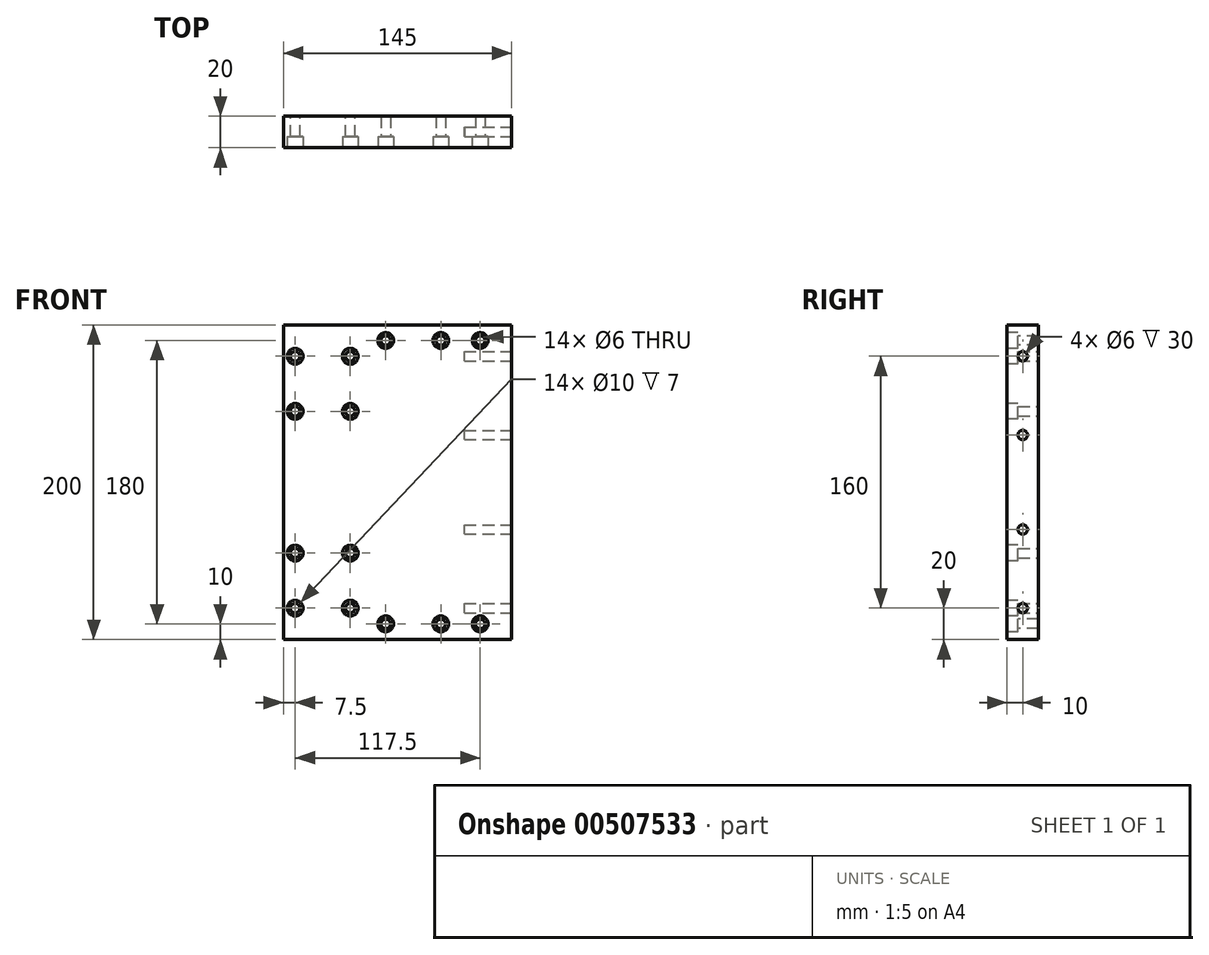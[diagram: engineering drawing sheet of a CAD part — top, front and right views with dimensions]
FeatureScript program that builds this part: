
annotation { "Feature Type Name" : "Feature", "Feature Type Description" : "" }
export const myFeature = defineFeature(function(context is Context, id is Id, definition is map)
    precondition{}
    {
        {
            var Q0;
            Q0=qCreatedBy(makeId("Front.planeOp"),FACE);
            var sketch = newSketch(context, id + "F0", { "sketchPlane" : qUnion([Q0])});
            skLineSegment(sketch, "E0.bottom", {"start": v(0, 0) * mm, "end": v(145, 0) * mm});
            skLineSegment(sketch, "E0.top", {"start": v(0, 200) * mm, "end": v(145, 200) * mm});
            skLineSegment(sketch, "E0.left", {"start": v(0, 0) * mm, "end": v(0, 200) * mm});
            skLineSegment(sketch, "E0.right", {"start": v(145, 0) * mm, "end": v(145, 200) * mm});
            skCircle(sketch, "E1", {"center": v(7.5, 20) * mm, "radius": 3 * mm});
            skCircle(sketch, "E2", {"center": v(7.5, 55) * mm, "radius": 3 * mm});
            skCircle(sketch, "E3", {"center": v(7.5, 145) * mm, "radius": 3 * mm});
            skCircle(sketch, "E4", {"center": v(7.5, 180) * mm, "radius": 3 * mm});
            skCircle(sketch, "E5", {"center": v(42.5, 20) * mm, "radius": 3 * mm});
            skCircle(sketch, "E6", {"center": v(42.5, 55) * mm, "radius": 3 * mm});
            skCircle(sketch, "E7", {"center": v(42.5, 145) * mm, "radius": 3 * mm});
            skCircle(sketch, "E8", {"center": v(42.5, 180) * mm, "radius": 3 * mm});
            skSolve(sketch);
        }
        {
            var Q0;
            Q0=makeQuery(id+"F0.imprint","IMPRINT",FACE,{"disambiguationData":[TD([[makeQuery(id+"F0.imprint","IMPRINT",EDGE,{"derivedFrom":sQuery(id+"F0.wireOp",EDGE,"E0.bottom")}),1.0]])]});
            extrude(context, id + "F1", {"entities" : qUnion([Q0]), "depth" : 20 * mm});
        }
        {
            var Q0;
            Q0=makeQuery(id+"F1.opExtrude","CAP_FACE",FACE,{"disambiguationData":[OSD([sQuery(id+"F0.wireOp",EDGE,"E0.bottom"),sQuery(id+"F0.wireOp",EDGE,"E0.top"),sQuery(id+"F0.wireOp",EDGE,"E0.left"),sQuery(id+"F0.wireOp",EDGE,"E0.right"),sQuery(id+"F0.wireOp",EDGE,"E1"),sQuery(id+"F0.wireOp",EDGE,"E2"),sQuery(id+"F0.wireOp",EDGE,"E3"),sQuery(id+"F0.wireOp",EDGE,"E4"),sQuery(id+"F0.wireOp",EDGE,"E5"),sQuery(id+"F0.wireOp",EDGE,"E6"),sQuery(id+"F0.wireOp",EDGE,"E7"),sQuery(id+"F0.wireOp",EDGE,"E8")])],"isStart":false});
            var sketch = newSketch(context, id + "F2", { "sketchPlane" : qUnion([Q0])});
            skCircle(sketch, "E9", {"center": v(7.5, 180) * mm, "radius": 5 * mm});
            skCircle(sketch, "E10", {"center": v(42.5, 180) * mm, "radius": 5 * mm});
            skCircle(sketch, "E11", {"center": v(7.5, 145) * mm, "radius": 5 * mm});
            skCircle(sketch, "E12", {"center": v(42.5, 145) * mm, "radius": 5 * mm});
            skCircle(sketch, "E13", {"center": v(7.5, 55) * mm, "radius": 5 * mm});
            skCircle(sketch, "E14", {"center": v(42.5, 55) * mm, "radius": 5 * mm});
            skCircle(sketch, "E15", {"center": v(7.5, 20) * mm, "radius": 5 * mm});
            skCircle(sketch, "E16", {"center": v(42.5, 20) * mm, "radius": 5 * mm});
            skSolve(sketch);
        }
        {
            var Q0;
            Q0 = qSketchRegion(id + "F2", true);
            extrude(context, id + "F3", {"entities" : qUnion([Q0]), "operationType" : NewBodyOperationType.REMOVE, "oppositeDirection" : true, "depth" : 7 * mm});
        }
        {
            var Q0;
            Q0=makeQuery(id+"F1.opExtrude","SWEPT_FACE",FACE,{"disambiguationData":[OSD([sQuery(id+"F0.wireOp",EDGE,"E0.right")])]});
            var sketch = newSketch(context, id + "F4", { "sketchPlane" : qUnion([Q0])});
            skCircle(sketch, "E17", {"center": v(-10, 20) * mm, "radius": 3 * mm});
            skCircle(sketch, "E18", {"center": v(-10, 70) * mm, "radius": 3 * mm});
            skCircle(sketch, "E19", {"center": v(-10, 130) * mm, "radius": 3 * mm});
            skCircle(sketch, "E20", {"center": v(-10, 180) * mm, "radius": 3 * mm});
            skSolve(sketch);
        }
        {
            var Q0;
            Q0 = qSketchRegion(id + "F4", true);
            extrude(context, id + "F5", {"entities" : qUnion([Q0]), "operationType" : NewBodyOperationType.REMOVE, "oppositeDirection" : true, "depth" : 30 * mm});
        }
        {
            var Q0;
            Q0=makeQuery(id+"F1.opExtrude","CAP_FACE",FACE,{"disambiguationData":[OSD([sQuery(id+"F0.wireOp",EDGE,"E0.bottom"),sQuery(id+"F0.wireOp",EDGE,"E0.top"),sQuery(id+"F0.wireOp",EDGE,"E0.left"),sQuery(id+"F0.wireOp",EDGE,"E0.right"),sQuery(id+"F0.wireOp",EDGE,"E1"),sQuery(id+"F0.wireOp",EDGE,"E2"),sQuery(id+"F0.wireOp",EDGE,"E3"),sQuery(id+"F0.wireOp",EDGE,"E4"),sQuery(id+"F0.wireOp",EDGE,"E5"),sQuery(id+"F0.wireOp",EDGE,"E6"),sQuery(id+"F0.wireOp",EDGE,"E7"),sQuery(id+"F0.wireOp",EDGE,"E8")])],"isStart":false});
            var sketch = newSketch(context, id + "F6", { "sketchPlane" : qUnion([Q0])});
            skCircle(sketch, "E21", {"center": v(125, 190) * mm, "radius": 3 * mm});
            skCircle(sketch, "E22", {"center": v(100, 190) * mm, "radius": 3 * mm});
            skCircle(sketch, "E23", {"center": v(65, 190) * mm, "radius": 3 * mm});
            skCircle(sketch, "E24", {"center": v(125, 10) * mm, "radius": 3 * mm});
            skCircle(sketch, "E25", {"center": v(100, 10) * mm, "radius": 3 * mm});
            skCircle(sketch, "E26", {"center": v(65, 10) * mm, "radius": 3 * mm});
            skSolve(sketch);
        }
        {
            var Q0;
            Q0 = qSketchRegion(id + "F6", true);
            extrude(context, id + "F7", {"entities" : qUnion([Q0]), "operationType" : NewBodyOperationType.REMOVE, "oppositeDirection" : true, "depth" : 20 * mm});
        }
        {
            var Q0;
            Q0=makeQuery(id+"F1.opExtrude","CAP_FACE",FACE,{"disambiguationData":[OSD([sQuery(id+"F0.wireOp",EDGE,"E0.bottom"),sQuery(id+"F0.wireOp",EDGE,"E0.top"),sQuery(id+"F0.wireOp",EDGE,"E0.left"),sQuery(id+"F0.wireOp",EDGE,"E0.right"),sQuery(id+"F0.wireOp",EDGE,"E1"),sQuery(id+"F0.wireOp",EDGE,"E2"),sQuery(id+"F0.wireOp",EDGE,"E3"),sQuery(id+"F0.wireOp",EDGE,"E4"),sQuery(id+"F0.wireOp",EDGE,"E5"),sQuery(id+"F0.wireOp",EDGE,"E6"),sQuery(id+"F0.wireOp",EDGE,"E7"),sQuery(id+"F0.wireOp",EDGE,"E8")])],"isStart":false});
            var sketch = newSketch(context, id + "F8", { "sketchPlane" : qUnion([Q0])});
            skCircle(sketch, "E27", {"center": v(65, 190) * mm, "radius": 5 * mm});
            skCircle(sketch, "E28", {"center": v(100, 190) * mm, "radius": 5 * mm});
            skCircle(sketch, "E29", {"center": v(125, 190) * mm, "radius": 5 * mm});
            skCircle(sketch, "E30", {"center": v(65, 10) * mm, "radius": 5 * mm});
            skCircle(sketch, "E31", {"center": v(100, 10) * mm, "radius": 5 * mm});
            skCircle(sketch, "E32", {"center": v(125, 10) * mm, "radius": 5 * mm});
            skSolve(sketch);
        }
        {
            var Q0;
            Q0 = qSketchRegion(id + "F8", true);
            extrude(context, id + "F9", {"entities" : qUnion([Q0]), "operationType" : NewBodyOperationType.REMOVE, "oppositeDirection" : true, "depth" : 7 * mm});
        }
    });
